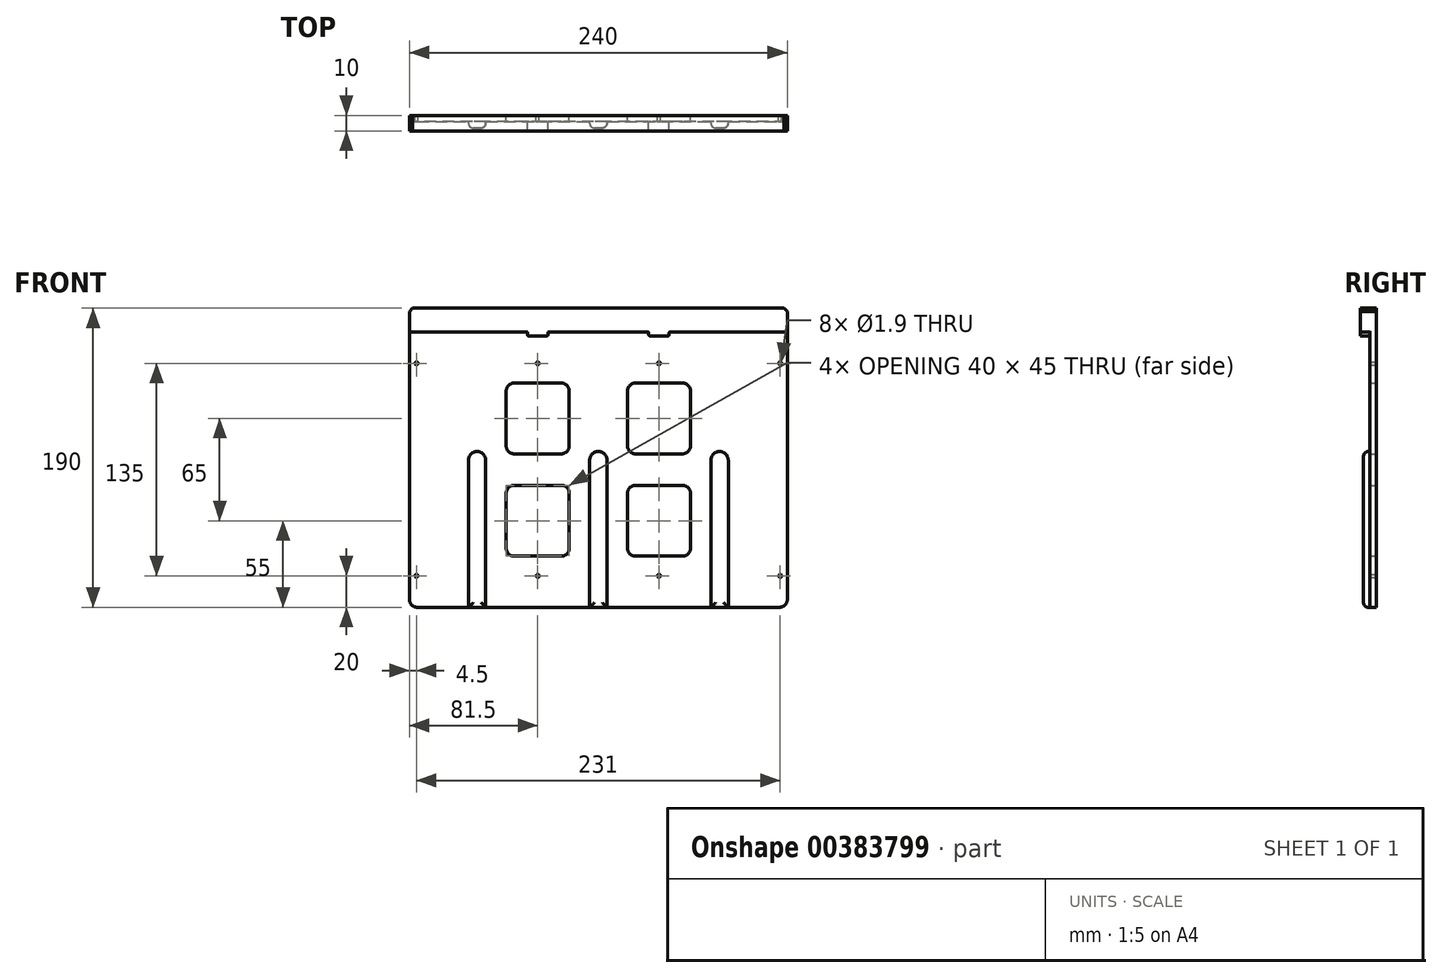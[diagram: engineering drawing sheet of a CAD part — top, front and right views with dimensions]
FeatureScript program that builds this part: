
annotation { "Feature Type Name" : "Feature", "Feature Type Description" : "" }
export const myFeature = defineFeature(function(context is Context, id is Id, definition is map)
    precondition{}
    {
        {
            var Q0;
            Q0=qCreatedBy(makeId("Front.planeOp"),FACE);
            var sketch = newSketch(context, id + "F0", { "sketchPlane" : qUnion([Q0])});
            skLineSegment(sketch, "E0.bottom", {"start": v(0, 0) * mm, "end": v(240, 0) * mm});
            skLineSegment(sketch, "E0.top", {"start": v(0, 190) * mm, "end": v(240, 190) * mm});
            skLineSegment(sketch, "E0.left", {"start": v(0, 0) * mm, "end": v(0, 190) * mm});
            skLineSegment(sketch, "E0.right", {"start": v(240, 0) * mm, "end": v(240, 190) * mm});
            skLineSegment(sketch, "E1", {"start": v(120, 190) * mm, "end": v(120, 0) * mm, "construction": true});
            skLineSegment(sketch, "E2", {"start": v(197, 190) * mm, "end": v(197, 0) * mm, "construction": true});
            skLineSegment(sketch, "E3", {"start": v(43, 190) * mm, "end": v(43, 0) * mm, "construction": true});
            skArc(sketch, "E4", {"start": v(48.5, 93.5) * mm, "mid": v(43, 99) * mm, "end": v(37.5, 93.5) * mm});
            skArc(sketch, "E5", {"start": v(125.5, 93.5) * mm, "mid": v(120, 99) * mm, "end": v(114.5, 93.5) * mm});
            skArc(sketch, "E6", {"start": v(202.5, 93.5) * mm, "mid": v(197, 99) * mm, "end": v(191.5, 93.5) * mm});
            skLineSegment(sketch, "E7", {"start": v(81.5, 190) * mm, "end": v(81.5, 0) * mm, "construction": true});
            skLineSegment(sketch, "E8", {"start": v(158.5, 190) * mm, "end": v(158.5, 0) * mm, "construction": true});
            skPoint(sketch, "E9.middle", {"position": v(81.5, 0) * mm});
            skLineSegment(sketch, "E10", {"start": v(37.5, 93.5) * mm, "end": v(37.5, 0) * mm});
            skLineSegment(sketch, "E11", {"start": v(48.5, 93.5) * mm, "end": v(48.5, 0) * mm});
            skLineSegment(sketch, "E12", {"start": v(114.5, 93.5) * mm, "end": v(114.5, 0) * mm});
            skLineSegment(sketch, "E13", {"start": v(125.5, 93.5) * mm, "end": v(125.5, 0) * mm});
            skLineSegment(sketch, "E14", {"start": v(191.5, 93.5) * mm, "end": v(191.5, 0) * mm});
            skLineSegment(sketch, "E15", {"start": v(202.5, 93.5) * mm, "end": v(202.5, 0) * mm});
            skLineSegment(sketch, "E16", {"start": v(0, 175) * mm, "end": v(240, 175) * mm, "construction": true});
            skLineSegment(sketch, "E17", {"start": v(75, 190) * mm, "end": v(75, 172.5) * mm});
            skLineSegment(sketch, "E18", {"start": v(75, 172.5) * mm, "end": v(88, 172.5) * mm});
            skLineSegment(sketch, "E19", {"start": v(88, 172.5) * mm, "end": v(88, 190) * mm});
            skLineSegment(sketch, "E20", {"start": v(152, 190) * mm, "end": v(152, 172.5) * mm});
            skLineSegment(sketch, "E21", {"start": v(152, 172.5) * mm, "end": v(165, 172.5) * mm});
            skLineSegment(sketch, "E22", {"start": v(165, 172.5) * mm, "end": v(165, 190) * mm});
            skLineSegment(sketch, "E23", {"start": v(235.5, 190) * mm, "end": v(235.5, 0) * mm, "construction": true});
            skLineSegment(sketch, "E24", {"start": v(4.5, 190) * mm, "end": v(4.5, 0) * mm, "construction": true});
            skCircle(sketch, "E25", {"center": v(4.5, 155) * mm, "radius": 0.95 * mm});
            skCircle(sketch, "E26", {"center": v(81.5, 155) * mm, "radius": 0.95 * mm});
            skCircle(sketch, "E27", {"center": v(158.5, 155) * mm, "radius": 0.95 * mm});
            skCircle(sketch, "E28", {"center": v(235.5, 155) * mm, "radius": 0.95 * mm});
            skCircle(sketch, "E29", {"center": v(4.5, 20) * mm, "radius": 0.95 * mm});
            skCircle(sketch, "E30", {"center": v(81.5, 20) * mm, "radius": 0.95 * mm});
            skCircle(sketch, "E31", {"center": v(158.5, 20) * mm, "radius": 0.95 * mm});
            skCircle(sketch, "E32", {"center": v(235.5, 20) * mm, "radius": 0.95 * mm});
            skLineSegment(sketch, "E33.bottom", {"start": v(101.5, 32.5) * mm, "end": v(61.5, 32.5) * mm});
            skLineSegment(sketch, "E33.top", {"start": v(101.5, 77.5) * mm, "end": v(61.5, 77.5) * mm});
            skLineSegment(sketch, "E33.left", {"start": v(101.5, 32.5) * mm, "end": v(101.5, 77.5) * mm});
            skLineSegment(sketch, "E33.right", {"start": v(61.5, 32.5) * mm, "end": v(61.5, 77.5) * mm});
            skPoint(sketch, "E33.middle", {"position": v(81.5, 55) * mm});
            skLineSegment(sketch, "E34.bottom", {"start": v(178.5, 32.5) * mm, "end": v(138.5, 32.5) * mm});
            skLineSegment(sketch, "E34.top", {"start": v(178.5, 77.5) * mm, "end": v(138.5, 77.5) * mm});
            skLineSegment(sketch, "E34.left", {"start": v(178.5, 32.5) * mm, "end": v(178.5, 77.5) * mm});
            skLineSegment(sketch, "E34.right", {"start": v(138.5, 32.5) * mm, "end": v(138.5, 77.5) * mm});
            skPoint(sketch, "E34.middle", {"position": v(158.5, 55) * mm});
            skLineSegment(sketch, "E35", {"start": v(0, 175) * mm, "end": v(75, 175) * mm});
            skLineSegment(sketch, "E36", {"start": v(88, 175) * mm, "end": v(152, 175) * mm});
            skLineSegment(sketch, "E37", {"start": v(165, 175) * mm, "end": v(240, 175) * mm});
            skLineSegment(sketch, "E38.bottom", {"start": v(101.5, 97.5) * mm, "end": v(61.5, 97.5) * mm});
            skLineSegment(sketch, "E38.top", {"start": v(101.5, 142.5) * mm, "end": v(61.5, 142.5) * mm});
            skLineSegment(sketch, "E38.left", {"start": v(101.5, 97.5) * mm, "end": v(101.5, 142.5) * mm});
            skLineSegment(sketch, "E38.right", {"start": v(61.5, 97.5) * mm, "end": v(61.5, 142.5) * mm});
            skPoint(sketch, "E38.middle", {"position": v(81.5, 120) * mm});
            skLineSegment(sketch, "E39.bottom", {"start": v(178.5, 97.5) * mm, "end": v(138.5, 97.5) * mm});
            skLineSegment(sketch, "E39.top", {"start": v(178.5, 142.5) * mm, "end": v(138.5, 142.5) * mm});
            skLineSegment(sketch, "E39.left", {"start": v(178.5, 97.5) * mm, "end": v(178.5, 142.5) * mm});
            skLineSegment(sketch, "E39.right", {"start": v(138.5, 97.5) * mm, "end": v(138.5, 142.5) * mm});
            skPoint(sketch, "E39.middle", {"position": v(158.5, 120) * mm});
            skSolve(sketch);
        }
        {
            var Q0;
            Q0=makeQuery(id+"F0.imprint","IMPRINT",FACE,{"disambiguationData":[TD([[makeQuery(id+"F0.imprint","IMPRINT",EDGE,{"derivedFrom":sQuery(id+"F0.wireOp",EDGE,"UCS8DdOD-ejyU-XilF-WruS-Bu7MYvNURBZs.bottom")}),-1.0]])]});
            var Q1;
            Q1=makeQuery(id+"F0.imprint","IMPRINT",FACE,{"disambiguationData":[TD([[makeQuery(id+"F0.imprint","IMPRINT",EDGE,{"derivedFrom":sQuery(id+"F0.wireOp",EDGE,"GRi4C73z-JWEP-kZG7-aWlK-krMTq5qBCM59.left")}),1.0]])]});
            var Q2;
            Q2=makeQuery(id+"F0.imprint","IMPRINT",FACE,{"disambiguationData":[TD([[makeQuery(id+"F0.imprint","IMPRINT",EDGE,{"derivedFrom":sQuery(id+"F0.wireOp",EDGE,"MJb00YoJ-KujM-1005-5pBj-Hys14JhzmI4w.left")}),1.0]])]});
            var Q3;
            Q3=makeQuery(id+"F0.imprint","IMPRINT",FACE,{"disambiguationData":[TD([[makeQuery(id+"F0.imprint","IMPRINT",EDGE,{"derivedFrom":sQuery(id+"F0.wireOp",EDGE,"MJb00YoJ-KujM-1005-5pBj-Hys14JhzmI4w.left")}),-1.0]])]});
            var Q4;
            Q4=makeQuery(id+"F0.imprint","IMPRINT",FACE,{"disambiguationData":[TD([[makeQuery(id+"F0.imprint","IMPRINT",EDGE,{"derivedFrom":sQuery(id+"F0.wireOp",EDGE,"SsHJZUVz-7gaE-nAlA-kBK5-nGGxjkbp80cZ.bottom")}),-1.0]])]});
            var Q5;
            {var subQ1=sQuery(id+"F0.wireOp",EDGE,"E0.right");Q5=makeQuery(id+"F0.imprint","IMPRINT",FACE,{"disambiguationData":[TD([[makeQuery(id+"F0.imprint","IMPRINT",EDGE,{"derivedFrom":subQ1}),1.0]])]});}
            var Q6;
            Q6=makeQuery(id+"F0.imprint","IMPRINT",FACE,{"disambiguationData":[TD([[makeQuery(id+"F0.imprint","IMPRINT",EDGE,{"derivedFrom":sQuery(id+"F0.wireOp",EDGE,"cF3qAKgA-6R1k-92Ln-ywlv-DPr7yGT8WVYd.left")}),1.0]])]});
            var Q7;
            {var subQ0=sQuery(id+"F0.wireOp",EDGE,"NWw21f8w-tgmn-euQu-w0p8-71T6GpV76rU4");Q7=makeQuery(id+"F0.imprint","IMPRINT",FACE,{"disambiguationData":[TD([[makeQuery(id+"F0.imprint","IMPRINT",EDGE,{"derivedFrom":subQ0}),-1.0]])]});}
            var Q8;
            {var subQ5=sQuery(id+"F0.wireOp",EDGE,"RuvmBQSr-5Cpm-upig-CqbM-MJYItVKPMDrs.bottom");Q8=makeQuery(id+"F0.imprint","IMPRINT",FACE,{"disambiguationData":[TD([[makeQuery(id+"F0.imprint","IMPRINT",EDGE,{"derivedFrom":subQ5}),1.0]])]});}
            var Q9;
            {var subQ5=sQuery(id+"F0.wireOp",EDGE,"E9.bottom");Q9=makeQuery(id+"F0.imprint","IMPRINT",FACE,{"disambiguationData":[TD([[makeQuery(id+"F0.imprint","IMPRINT",EDGE,{"derivedFrom":subQ5}),1.0]])]});}
            var Q10;
            Q10=makeQuery(id+"F0.imprint","IMPRINT",FACE,{"disambiguationData":[TD([[makeQuery(id+"F0.imprint","IMPRINT",EDGE,{"derivedFrom":sQuery(id+"F0.wireOp",EDGE,"XTZR7JBc-rO7E-wzYZ-XdEQ-IZ1jBMIKU54G.bottom")}),-1.0]])]});
            var Q11;
            Q11=makeQuery(id+"F0.imprint","IMPRINT",FACE,{"disambiguationData":[TD([[makeQuery(id+"F0.imprint","IMPRINT",EDGE,{"derivedFrom":sQuery(id+"F0.wireOp",EDGE,"QuKBfMWp-nAjc-eiIa-FsoC-LC1ooK1glI0I.bottom")}),-1.0]])]});
            var Q12;
            Q12=makeQuery(id+"F0.imprint","IMPRINT",FACE,{"disambiguationData":[TD([[makeQuery(id+"F0.imprint","IMPRINT",EDGE,{"derivedFrom":sQuery(id+"F0.wireOp",EDGE,"zr7SBste-XHF5-nfNJ-ePE3-pIRu4rkJVY1c.bottom")}),-1.0]])]});
            var Q13;
            Q13=makeQuery(id+"F0.imprint","IMPRINT",FACE,{"disambiguationData":[TD([[makeQuery(id+"F0.imprint","IMPRINT",EDGE,{"derivedFrom":sQuery(id+"F0.wireOp",EDGE,"EneNzpn4-2OMr-KFmW-9g9d-3BS7Mlzjb1r9.bottom")}),-1.0]])]});
            var Q14;
            {var subQ0=sQuery(id+"F0.wireOp",EDGE,"mL9XTioa-9DpA-IpuZ-Q8Eg-WP72gxXpwuHZ.bottom");var subQ1=sQuery(id+"F0.wireOp",EDGE,"SsHJZUVz-7gaE-nAlA-kBK5-nGGxjkbp80cZ.left");var subQ2=makeQuery(id+"F0.imprint","INTERSECT",VERTEX,{"derivedFrom":[subQ1,subQ0]});Q14=makeQuery(id+"F0.imprint","IMPRINT",FACE,{"disambiguationData":[TD([[makeQuery(id+"F0.imprint","IMPRINT",EDGE,{"disambiguationData":[TD([[subQ2,-1.0]])],"derivedFrom":subQ1}),-1.0]])]});}
            var Q15;
            {var subQ5=sQuery(id+"F0.wireOp",EDGE,"m287s5nx-l1Bl-8Bmj-dwCZ-KAfyaVMRRT36.top");Q15=makeQuery(id+"F0.imprint","IMPRINT",FACE,{"disambiguationData":[TD([[makeQuery(id+"F0.imprint","IMPRINT",EDGE,{"derivedFrom":subQ5}),-1.0]])]});}
            var Q16;
            {var subQ5=sQuery(id+"F0.wireOp",EDGE,"mL9XTioa-9DpA-IpuZ-Q8Eg-WP72gxXpwuHZ.left");Q16=makeQuery(id+"F0.imprint","IMPRINT",FACE,{"disambiguationData":[TD([[makeQuery(id+"F0.imprint","IMPRINT",EDGE,{"derivedFrom":subQ5}),1.0]])]});}
            var Q17;
            {var subQ0=sQuery(id+"F0.wireOp",EDGE,"mL9XTioa-9DpA-IpuZ-Q8Eg-WP72gxXpwuHZ.bottom");var subQ1=sQuery(id+"F0.wireOp",EDGE,"SsHJZUVz-7gaE-nAlA-kBK5-nGGxjkbp80cZ.left");var subQ2=makeQuery(id+"F0.imprint","INTERSECT",VERTEX,{"derivedFrom":[subQ1,subQ0]});Q17=makeQuery(id+"F0.imprint","IMPRINT",FACE,{"disambiguationData":[TD([[makeQuery(id+"F0.imprint","IMPRINT",EDGE,{"disambiguationData":[TD([[subQ2,-1.0]])],"derivedFrom":subQ1}),1.0]])]});}
            var Q18;
            {var subQ3=sQuery(id+"F0.wireOp",EDGE,"8tIIhmZ9-kIaI-KP0b-BDpp-fG9OmIQPOIbA.top");Q18=makeQuery(id+"F0.imprint","IMPRINT",FACE,{"disambiguationData":[TD([[makeQuery(id+"F0.imprint","IMPRINT",EDGE,{"derivedFrom":subQ3}),-1.0]])]});}
            var Q19;
            {var subQ5=sQuery(id+"F0.wireOp",EDGE,"mL9XTioa-9DpA-IpuZ-Q8Eg-WP72gxXpwuHZ.right");Q19=makeQuery(id+"F0.imprint","IMPRINT",FACE,{"disambiguationData":[TD([[makeQuery(id+"F0.imprint","IMPRINT",EDGE,{"derivedFrom":subQ5}),-1.0]])]});}
            var Q20;
            Q20=makeQuery(id+"F0.imprint","IMPRINT",FACE,{"disambiguationData":[TD([[makeQuery(id+"F0.imprint","IMPRINT",EDGE,{"derivedFrom":sQuery(id+"F0.wireOp",EDGE,"m287s5nx-l1Bl-8Bmj-dwCZ-KAfyaVMRRT36.bottom")}),-1.0]])]});
            var Q21;
            Q21=makeQuery(id+"F0.imprint","IMPRINT",FACE,{"disambiguationData":[TD([[makeQuery(id+"F0.imprint","IMPRINT",EDGE,{"derivedFrom":sQuery(id+"F0.wireOp",EDGE,"8tIIhmZ9-kIaI-KP0b-BDpp-fG9OmIQPOIbA.bottom")}),-1.0]])]});
            var Q22;
            {var subQ0=sQuery(id+"F0.wireOp",EDGE,"E20");var subQ1=sQuery(id+"F0.wireOp",EDGE,"E0.top");var subQ2=makeQuery(id+"F0.imprint","INTERSECT",VERTEX,{"derivedFrom":[subQ1,subQ0]});Q22=makeQuery(id+"F0.imprint","IMPRINT",FACE,{"disambiguationData":[TD([[makeQuery(id+"F0.imprint","IMPRINT",EDGE,{"disambiguationData":[TD([[subQ2,-1.0]])],"derivedFrom":subQ1}),-1.0]])]});}
            var Q23;
            {var subQ5=sQuery(id+"F0.wireOp",EDGE,"E21");Q23=makeQuery(id+"F0.imprint","IMPRINT",FACE,{"disambiguationData":[TD([[makeQuery(id+"F0.imprint","IMPRINT",EDGE,{"derivedFrom":subQ5}),1.0]])]});}
            var Q24;
            {var subQ0=sQuery(id+"F0.wireOp",EDGE,"E19");var subQ1=sQuery(id+"F0.wireOp",EDGE,"E0.top");var subQ2=makeQuery(id+"F0.imprint","INTERSECT",VERTEX,{"derivedFrom":[subQ1,subQ0]});Q24=makeQuery(id+"F0.imprint","IMPRINT",FACE,{"disambiguationData":[TD([[makeQuery(id+"F0.imprint","IMPRINT",EDGE,{"disambiguationData":[TD([[subQ2,-1.0]])],"derivedFrom":subQ1}),-1.0]])]});}
            var Q25;
            Q25=makeQuery(id+"F0.imprint","IMPRINT",FACE,{"disambiguationData":[TD([[makeQuery(id+"F0.imprint","IMPRINT",EDGE,{"derivedFrom":sQuery(id+"F0.wireOp",EDGE,"E4")}),-1.0]])]});
            var Q26;
            {var subQ5=sQuery(id+"F0.wireOp",EDGE,"E18");Q26=makeQuery(id+"F0.imprint","IMPRINT",FACE,{"disambiguationData":[TD([[makeQuery(id+"F0.imprint","IMPRINT",EDGE,{"derivedFrom":subQ5}),1.0]])]});}
            var Q27;
            {var subQ0=sQuery(id+"F0.wireOp",EDGE,"E17");var subQ1=sQuery(id+"F0.wireOp",EDGE,"E0.top");var subQ2=makeQuery(id+"F0.imprint","INTERSECT",VERTEX,{"derivedFrom":[subQ1,subQ0]});Q27=makeQuery(id+"F0.imprint","IMPRINT",FACE,{"disambiguationData":[TD([[makeQuery(id+"F0.imprint","IMPRINT",EDGE,{"disambiguationData":[TD([[subQ2,-1.0]])],"derivedFrom":subQ1}),-1.0]])]});}
            var Q28;
            {var subQ0=sQuery(id+"F0.wireOp",EDGE,"E0.left");var subQ1=sQuery(id+"F0.wireOp",EDGE,"E0.top");var subQ2=makeQuery(id+"F0.imprint","INTERSECT",VERTEX,{"derivedFrom":[subQ1,subQ0]});Q28=makeQuery(id+"F0.imprint","IMPRINT",FACE,{"disambiguationData":[TD([[makeQuery(id+"F0.imprint","IMPRINT",EDGE,{"disambiguationData":[TD([[subQ2,-1.0]])],"derivedFrom":subQ1}),-1.0]])]});}
            var Q29;
            Q29=makeQuery(id+"F0.imprint","IMPRINT",FACE,{"disambiguationData":[TD([[makeQuery(id+"F0.imprint","IMPRINT",EDGE,{"derivedFrom":sQuery(id+"F0.wireOp",EDGE,"E4")}),1.0]])]});
            var Q30;
            Q30=makeQuery(id+"F0.imprint","IMPRINT",FACE,{"disambiguationData":[TD([[makeQuery(id+"F0.imprint","IMPRINT",EDGE,{"derivedFrom":sQuery(id+"F0.wireOp",EDGE,"E5")}),1.0]])]});
            var Q31;
            Q31=makeQuery(id+"F0.imprint","IMPRINT",FACE,{"disambiguationData":[TD([[makeQuery(id+"F0.imprint","IMPRINT",EDGE,{"derivedFrom":sQuery(id+"F0.wireOp",EDGE,"E6")}),1.0]])]});
            extrude(context, id + "F1", {"entities" : qUnion([Q0, Q1, Q2, Q3, Q4, Q5, Q6, Q7, Q8, Q9, Q10, Q11, Q12, Q13, Q14, Q15, Q16, Q17, Q18, Q19, Q20, Q21, Q22, Q23, Q24, Q25, Q26, Q27, Q28, Q29, Q30, Q31]), "depth" : 4 * mm});
        }
        {
            var Q0;
            {var subQ0=sQuery(id+"F0.wireOp",EDGE,"mL9XTioa-9DpA-IpuZ-Q8Eg-WP72gxXpwuHZ.bottom");var subQ1=sQuery(id+"F0.wireOp",EDGE,"NWw21f8w-tgmn-euQu-w0p8-71T6GpV76rU4");var subQ2=makeQuery(id+"F0.imprint","INTERSECT",VERTEX,{"derivedFrom":[subQ1,subQ0]});Q0=makeQuery(id+"F0.imprint","IMPRINT",FACE,{"disambiguationData":[TD([[makeQuery(id+"F0.imprint","IMPRINT",EDGE,{"disambiguationData":[TD([[subQ2,-1.0]])],"derivedFrom":subQ1}),-1.0]])]});}
            var Q1;
            {var subQ5=sQuery(id+"F0.wireOp",EDGE,"m287s5nx-l1Bl-8Bmj-dwCZ-KAfyaVMRRT36.top");Q1=makeQuery(id+"F0.imprint","IMPRINT",FACE,{"disambiguationData":[TD([[makeQuery(id+"F0.imprint","IMPRINT",EDGE,{"derivedFrom":subQ5}),-1.0]])]});}
            var Q2;
            {var subQ5=sQuery(id+"F0.wireOp",EDGE,"mL9XTioa-9DpA-IpuZ-Q8Eg-WP72gxXpwuHZ.left");Q2=makeQuery(id+"F0.imprint","IMPRINT",FACE,{"disambiguationData":[TD([[makeQuery(id+"F0.imprint","IMPRINT",EDGE,{"derivedFrom":subQ5}),1.0]])]});}
            var Q3;
            {var subQ0=sQuery(id+"F0.wireOp",EDGE,"mL9XTioa-9DpA-IpuZ-Q8Eg-WP72gxXpwuHZ.bottom");var subQ1=sQuery(id+"F0.wireOp",EDGE,"SsHJZUVz-7gaE-nAlA-kBK5-nGGxjkbp80cZ.left");var subQ2=makeQuery(id+"F0.imprint","INTERSECT",VERTEX,{"derivedFrom":[subQ1,subQ0]});Q3=makeQuery(id+"F0.imprint","IMPRINT",FACE,{"disambiguationData":[TD([[makeQuery(id+"F0.imprint","IMPRINT",EDGE,{"disambiguationData":[TD([[subQ2,-1.0]])],"derivedFrom":subQ1}),-1.0]])]});}
            var Q4;
            {var subQ0=sQuery(id+"F0.wireOp",EDGE,"mL9XTioa-9DpA-IpuZ-Q8Eg-WP72gxXpwuHZ.bottom");var subQ1=sQuery(id+"F0.wireOp",EDGE,"SsHJZUVz-7gaE-nAlA-kBK5-nGGxjkbp80cZ.left");var subQ2=makeQuery(id+"F0.imprint","INTERSECT",VERTEX,{"derivedFrom":[subQ1,subQ0]});Q4=makeQuery(id+"F0.imprint","IMPRINT",FACE,{"disambiguationData":[TD([[makeQuery(id+"F0.imprint","IMPRINT",EDGE,{"disambiguationData":[TD([[subQ2,-1.0]])],"derivedFrom":subQ1}),1.0]])]});}
            var Q5;
            {var subQ3=sQuery(id+"F0.wireOp",EDGE,"8tIIhmZ9-kIaI-KP0b-BDpp-fG9OmIQPOIbA.top");Q5=makeQuery(id+"F0.imprint","IMPRINT",FACE,{"disambiguationData":[TD([[makeQuery(id+"F0.imprint","IMPRINT",EDGE,{"derivedFrom":subQ3}),-1.0]])]});}
            var Q6;
            {var subQ5=sQuery(id+"F0.wireOp",EDGE,"mL9XTioa-9DpA-IpuZ-Q8Eg-WP72gxXpwuHZ.right");Q6=makeQuery(id+"F0.imprint","IMPRINT",FACE,{"disambiguationData":[TD([[makeQuery(id+"F0.imprint","IMPRINT",EDGE,{"derivedFrom":subQ5}),-1.0]])]});}
            var Q7;
            {var subQ5=sQuery(id+"F0.wireOp",EDGE,"RuvmBQSr-5Cpm-upig-CqbM-MJYItVKPMDrs.bottom");Q7=makeQuery(id+"F0.imprint","IMPRINT",FACE,{"disambiguationData":[TD([[makeQuery(id+"F0.imprint","IMPRINT",EDGE,{"derivedFrom":subQ5}),1.0]])]});}
            var Q8;
            {var subQ5=sQuery(id+"F0.wireOp",EDGE,"E9.bottom");Q8=makeQuery(id+"F0.imprint","IMPRINT",FACE,{"disambiguationData":[TD([[makeQuery(id+"F0.imprint","IMPRINT",EDGE,{"derivedFrom":subQ5}),1.0]])]});}
            var Q9;
            Q9=makeQuery(id+"F0.imprint","IMPRINT",FACE,{"disambiguationData":[TD([[makeQuery(id+"F0.imprint","IMPRINT",EDGE,{"derivedFrom":sQuery(id+"F0.wireOp",EDGE,"MJb00YoJ-KujM-1005-5pBj-Hys14JhzmI4w.left")}),1.0]])]});
            var Q10;
            Q10=makeQuery(id+"F0.imprint","IMPRINT",FACE,{"disambiguationData":[TD([[makeQuery(id+"F0.imprint","IMPRINT",EDGE,{"derivedFrom":sQuery(id+"F0.wireOp",EDGE,"cF3qAKgA-6R1k-92Ln-ywlv-DPr7yGT8WVYd.left")}),1.0]])]});
            var Q11;
            Q11=makeQuery(id+"F0.imprint","IMPRINT",FACE,{"disambiguationData":[TD([[makeQuery(id+"F0.imprint","IMPRINT",EDGE,{"derivedFrom":sQuery(id+"F0.wireOp",EDGE,"GRi4C73z-JWEP-kZG7-aWlK-krMTq5qBCM59.left")}),1.0]])]});
            var Q12;
            Q12=makeQuery(id+"F0.imprint","IMPRINT",FACE,{"disambiguationData":[TD([[makeQuery(id+"F0.imprint","IMPRINT",EDGE,{"derivedFrom":sQuery(id+"F0.wireOp",EDGE,"E4")}),1.0]])]});
            var Q13;
            Q13=makeQuery(id+"F0.imprint","IMPRINT",FACE,{"disambiguationData":[TD([[makeQuery(id+"F0.imprint","IMPRINT",EDGE,{"derivedFrom":sQuery(id+"F0.wireOp",EDGE,"E5")}),1.0]])]});
            var Q14;
            Q14=makeQuery(id+"F0.imprint","IMPRINT",FACE,{"disambiguationData":[TD([[makeQuery(id+"F0.imprint","IMPRINT",EDGE,{"derivedFrom":sQuery(id+"F0.wireOp",EDGE,"E6")}),1.0]])]});
            var Q15;
            Q15=sQuery(id+"F0.wireOp",EDGE,"GRi4C73z-JWEP-kZG7-aWlK-krMTq5qBCM59.right");
            var Q16;
            Q16=sQuery(id+"F0.wireOp",EDGE,"E4");
            var Q17;
            Q17=sQuery(id+"F0.wireOp",EDGE,"GRi4C73z-JWEP-kZG7-aWlK-krMTq5qBCM59.left");
            var Q18;
            Q18=sQuery(id+"F0.wireOp",EDGE,"cZHNsq4v-RjbF-qvnB-klJb-ReqYlpQdkK8d");
            var Q19;
            Q19=sQuery(id+"F0.wireOp",EDGE,"WpUKDbhN-TVkI-Cn0c-r8IW-TSZfF7SMHj3x");
            extrude(context, id + "F2", {"entities" : qUnion([Q0, Q1, Q2, Q3, Q4, Q5, Q6, Q7, Q8, Q9, Q10, Q11, Q12, Q13, Q14]), "operationType" : NewBodyOperationType.ADD, "surfaceEntities" : qUnion([Q15, Q16, Q17, Q18, Q19]), "depth" : 8 * mm});
        }
        {
            var Q0;
            {var subQ0=sQuery(id+"F0.wireOp",EDGE,"E17");var subQ1=sQuery(id+"F0.wireOp",EDGE,"E0.top");var subQ2=makeQuery(id+"F0.imprint","INTERSECT",VERTEX,{"derivedFrom":[subQ1,subQ0]});Q0=makeQuery(id+"F0.imprint","IMPRINT",FACE,{"disambiguationData":[TD([[makeQuery(id+"F0.imprint","IMPRINT",EDGE,{"disambiguationData":[TD([[subQ2,-1.0]])],"derivedFrom":subQ1}),-1.0]])]});}
            var Q1;
            {var subQ5=sQuery(id+"F0.wireOp",EDGE,"E18");Q1=makeQuery(id+"F0.imprint","IMPRINT",FACE,{"disambiguationData":[TD([[makeQuery(id+"F0.imprint","IMPRINT",EDGE,{"derivedFrom":subQ5}),1.0]])]});}
            var Q2;
            {var subQ5=sQuery(id+"F0.wireOp",EDGE,"E21");Q2=makeQuery(id+"F0.imprint","IMPRINT",FACE,{"disambiguationData":[TD([[makeQuery(id+"F0.imprint","IMPRINT",EDGE,{"derivedFrom":subQ5}),1.0]])]});}
            var Q3;
            {var subQ0=sQuery(id+"F0.wireOp",EDGE,"E20");var subQ1=sQuery(id+"F0.wireOp",EDGE,"E0.top");var subQ2=makeQuery(id+"F0.imprint","INTERSECT",VERTEX,{"derivedFrom":[subQ1,subQ0]});Q3=makeQuery(id+"F0.imprint","IMPRINT",FACE,{"disambiguationData":[TD([[makeQuery(id+"F0.imprint","IMPRINT",EDGE,{"disambiguationData":[TD([[subQ2,-1.0]])],"derivedFrom":subQ1}),-1.0]])]});}
            var Q4;
            {var subQ5=sQuery(id+"F0.wireOp",EDGE,"E37");Q4=makeQuery(id+"F0.imprint","IMPRINT",FACE,{"disambiguationData":[TD([[makeQuery(id+"F0.imprint","IMPRINT",EDGE,{"derivedFrom":subQ5}),1.0]])]});}
            var Q5;
            {var subQ5=sQuery(id+"F0.wireOp",EDGE,"E36");Q5=makeQuery(id+"F0.imprint","IMPRINT",FACE,{"disambiguationData":[TD([[makeQuery(id+"F0.imprint","IMPRINT",EDGE,{"derivedFrom":subQ5}),1.0]])]});}
            var Q6;
            {var subQ5=sQuery(id+"F0.wireOp",EDGE,"E35");Q6=makeQuery(id+"F0.imprint","IMPRINT",FACE,{"disambiguationData":[TD([[makeQuery(id+"F0.imprint","IMPRINT",EDGE,{"derivedFrom":subQ5}),1.0]])]});}
            extrude(context, id + "F3", {"entities" : qUnion([Q0, Q1, Q2, Q3, Q4, Q5, Q6]), "operationType" : NewBodyOperationType.ADD, "depth" : 10 * mm});
        }
        {
            var Q0;
            Q0=makeQuery(id+"F1.opExtrude","SWEPT_EDGE",EDGE,{"disambiguationData":[OSD([sQuery(id+"F0.wireOp",EDGE,"E0.bottom"),sQuery(id+"F0.wireOp",EDGE,"E0.left")])]});
            var Q1;
            Q1=makeQuery(id+"F1.opExtrude","SWEPT_EDGE",EDGE,{"disambiguationData":[OSD([sQuery(id+"F0.wireOp",EDGE,"E0.bottom"),sQuery(id+"F0.wireOp",EDGE,"E0.right")])]});
            var Q2;
            Q2=makeQuery(id+"F1.opExtrude","SWEPT_EDGE",EDGE,{"disambiguationData":[OSD([sQuery(id+"F0.wireOp",EDGE,"E34.bottom"),sQuery(id+"F0.wireOp",EDGE,"E34.right")])]});
            var Q3;
            Q3=makeQuery(id+"F1.opExtrude","SWEPT_EDGE",EDGE,{"disambiguationData":[OSD([sQuery(id+"F0.wireOp",EDGE,"E34.bottom"),sQuery(id+"F0.wireOp",EDGE,"E34.left")])]});
            var Q4;
            Q4=makeQuery(id+"F1.opExtrude","SWEPT_EDGE",EDGE,{"disambiguationData":[OSD([sQuery(id+"F0.wireOp",EDGE,"E34.top"),sQuery(id+"F0.wireOp",EDGE,"E34.left")])]});
            var Q5;
            Q5=makeQuery(id+"F1.opExtrude","SWEPT_EDGE",EDGE,{"disambiguationData":[OSD([sQuery(id+"F0.wireOp",EDGE,"E34.top"),sQuery(id+"F0.wireOp",EDGE,"E34.right")])]});
            var Q6;
            Q6=makeQuery(id+"F1.opExtrude","SWEPT_EDGE",EDGE,{"disambiguationData":[OSD([sQuery(id+"F0.wireOp",EDGE,"E39.top"),sQuery(id+"F0.wireOp",EDGE,"E39.right")])]});
            var Q7;
            Q7=makeQuery(id+"F1.opExtrude","SWEPT_EDGE",EDGE,{"disambiguationData":[OSD([sQuery(id+"F0.wireOp",EDGE,"E39.top"),sQuery(id+"F0.wireOp",EDGE,"E39.left")])]});
            var Q8;
            Q8=makeQuery(id+"F1.opExtrude","SWEPT_EDGE",EDGE,{"disambiguationData":[OSD([sQuery(id+"F0.wireOp",EDGE,"E39.bottom"),sQuery(id+"F0.wireOp",EDGE,"E39.left")])]});
            var Q9;
            Q9=makeQuery(id+"F1.opExtrude","SWEPT_EDGE",EDGE,{"disambiguationData":[OSD([sQuery(id+"F0.wireOp",EDGE,"E39.bottom"),sQuery(id+"F0.wireOp",EDGE,"E39.right")])]});
            var Q10;
            Q10=makeQuery(id+"F1.opExtrude","SWEPT_EDGE",EDGE,{"disambiguationData":[OSD([sQuery(id+"F0.wireOp",EDGE,"E33.bottom"),sQuery(id+"F0.wireOp",EDGE,"E33.right")])]});
            var Q11;
            Q11=makeQuery(id+"F1.opExtrude","SWEPT_EDGE",EDGE,{"disambiguationData":[OSD([sQuery(id+"F0.wireOp",EDGE,"E33.bottom"),sQuery(id+"F0.wireOp",EDGE,"E33.left")])]});
            var Q12;
            Q12=makeQuery(id+"F1.opExtrude","SWEPT_EDGE",EDGE,{"disambiguationData":[OSD([sQuery(id+"F0.wireOp",EDGE,"E33.top"),sQuery(id+"F0.wireOp",EDGE,"E33.left")])]});
            var Q13;
            Q13=makeQuery(id+"F1.opExtrude","SWEPT_EDGE",EDGE,{"disambiguationData":[OSD([sQuery(id+"F0.wireOp",EDGE,"E33.top"),sQuery(id+"F0.wireOp",EDGE,"E33.right")])]});
            var Q14;
            Q14=makeQuery(id+"F1.opExtrude","SWEPT_EDGE",EDGE,{"disambiguationData":[OSD([sQuery(id+"F0.wireOp",EDGE,"E38.bottom"),sQuery(id+"F0.wireOp",EDGE,"E38.left")])]});
            var Q15;
            Q15=makeQuery(id+"F1.opExtrude","SWEPT_EDGE",EDGE,{"disambiguationData":[OSD([sQuery(id+"F0.wireOp",EDGE,"E38.top"),sQuery(id+"F0.wireOp",EDGE,"E38.left")])]});
            var Q16;
            Q16=makeQuery(id+"F1.opExtrude","SWEPT_EDGE",EDGE,{"disambiguationData":[OSD([sQuery(id+"F0.wireOp",EDGE,"E38.top"),sQuery(id+"F0.wireOp",EDGE,"E38.right")])]});
            var Q17;
            Q17=makeQuery(id+"F1.opExtrude","SWEPT_EDGE",EDGE,{"disambiguationData":[OSD([sQuery(id+"F0.wireOp",EDGE,"E38.bottom"),sQuery(id+"F0.wireOp",EDGE,"E38.right")])]});
            fillet(context, id + "F4", {"entities" : qUnion([Q0, Q1, Q2, Q3, Q4, Q5, Q6, Q7, Q8, Q9, Q10, Q11, Q12, Q13, Q14, Q15, Q16, Q17]), "radius" : 5 * mm, "tangentPropagation" : true, "allowEdgeOverflow" : false});
        }
        {
            var Q0;
            {var subQ0=sQuery(id+"F0.wireOp",EDGE,"E0.right");var subQ1=sQuery(id+"F0.wireOp",EDGE,"E0.top");Q0=makeQuery(id+"F3.boolean.opBoolean","MERGE",EDGE,{"derivedFrom":[makeQuery(id+"F1.opExtrude","SWEPT_EDGE",EDGE,{"disambiguationData":[OSD([subQ1,subQ0])]}),makeQuery(id+"F3.opExtrude","SWEPT_EDGE",EDGE,{"disambiguationData":[OSD([subQ1,subQ0])]})]});}
            var Q1;
            {var subQ0=sQuery(id+"F0.wireOp",EDGE,"E0.left");var subQ1=sQuery(id+"F0.wireOp",EDGE,"E0.top");Q1=makeQuery(id+"F3.boolean.opBoolean","MERGE",EDGE,{"derivedFrom":[makeQuery(id+"F1.opExtrude","SWEPT_EDGE",EDGE,{"disambiguationData":[OSD([subQ1,subQ0])]}),makeQuery(id+"F3.opExtrude","SWEPT_EDGE",EDGE,{"disambiguationData":[OSD([subQ1,subQ0])]})]});}
            chamfer(context, id + "F5", {"entities" : qUnion([Q0, Q1]), "width" : 2 * mm, "tangentPropagation" : true});
        }
        {
            var Q0;
            Q0=makeQuery(id+"F2.opExtrude","CAP_FACE",FACE,{"disambiguationData":[OSD([sQuery(id+"F0.wireOp",EDGE,"E0.bottom"),sQuery(id+"F0.wireOp",EDGE,"E4"),sQuery(id+"F0.wireOp",EDGE,"E10"),sQuery(id+"F0.wireOp",EDGE,"E11")])],"isStart":false});
            var Q1;
            Q1=makeQuery(id+"F2.opExtrude","CAP_FACE",FACE,{"disambiguationData":[OSD([sQuery(id+"F0.wireOp",EDGE,"E0.bottom"),sQuery(id+"F0.wireOp",EDGE,"E5"),sQuery(id+"F0.wireOp",EDGE,"E12"),sQuery(id+"F0.wireOp",EDGE,"E13")])],"isStart":false});
            var Q2;
            Q2=makeQuery(id+"F2.opExtrude","CAP_FACE",FACE,{"disambiguationData":[OSD([sQuery(id+"F0.wireOp",EDGE,"E0.bottom"),sQuery(id+"F0.wireOp",EDGE,"E6"),sQuery(id+"F0.wireOp",EDGE,"E14"),sQuery(id+"F0.wireOp",EDGE,"E15")])],"isStart":false});
            fillet(context, id + "F6", {"entities" : qUnion([Q0, Q1, Q2]), "radius" : 3 * mm, "tangentPropagation" : true, "allowEdgeOverflow" : false});
        }
        {
            var Q0;
            Q0=makeQuery(id+"F3.opExtrude","SWEPT_EDGE",EDGE,{"disambiguationData":[OSD([sQuery(id+"F0.wireOp",EDGE,"E17"),sQuery(id+"F0.wireOp",EDGE,"E18")])]});
            var Q1;
            Q1=makeQuery(id+"F3.opExtrude","SWEPT_EDGE",EDGE,{"disambiguationData":[OSD([sQuery(id+"F0.wireOp",EDGE,"E17"),sQuery(id+"F0.wireOp",EDGE,"E35")])]});
            var Q2;
            Q2=makeQuery(id+"F3.opExtrude","SWEPT_EDGE",EDGE,{"disambiguationData":[OSD([sQuery(id+"F0.wireOp",EDGE,"E18"),sQuery(id+"F0.wireOp",EDGE,"E19")])]});
            var Q3;
            Q3=makeQuery(id+"F3.opExtrude","SWEPT_EDGE",EDGE,{"disambiguationData":[OSD([sQuery(id+"F0.wireOp",EDGE,"E19"),sQuery(id+"F0.wireOp",EDGE,"E36")])]});
            var Q4;
            Q4=makeQuery(id+"F3.opExtrude","SWEPT_EDGE",EDGE,{"disambiguationData":[OSD([sQuery(id+"F0.wireOp",EDGE,"E20"),sQuery(id+"F0.wireOp",EDGE,"E36")])]});
            var Q5;
            Q5=makeQuery(id+"F3.opExtrude","SWEPT_EDGE",EDGE,{"disambiguationData":[OSD([sQuery(id+"F0.wireOp",EDGE,"E20"),sQuery(id+"F0.wireOp",EDGE,"E21")])]});
            var Q6;
            Q6=makeQuery(id+"F3.opExtrude","SWEPT_EDGE",EDGE,{"disambiguationData":[OSD([sQuery(id+"F0.wireOp",EDGE,"E21"),sQuery(id+"F0.wireOp",EDGE,"E22")])]});
            var Q7;
            Q7=makeQuery(id+"F3.opExtrude","SWEPT_EDGE",EDGE,{"disambiguationData":[OSD([sQuery(id+"F0.wireOp",EDGE,"E22"),sQuery(id+"F0.wireOp",EDGE,"E37")])]});
            var Q8;
            Q8=makeQuery(id+"F3.opExtrude","SWEPT_EDGE",EDGE,{"disambiguationData":[OSD([sQuery(id+"F0.wireOp",EDGE,"E0.right"),sQuery(id+"F0.wireOp",EDGE,"E37")])]});
            var Q9;
            Q9=makeQuery(id+"F3.opExtrude","SWEPT_EDGE",EDGE,{"disambiguationData":[OSD([sQuery(id+"F0.wireOp",EDGE,"E0.left"),sQuery(id+"F0.wireOp",EDGE,"E35")])]});
            fillet(context, id + "F7", {"entities" : qUnion([Q0, Q1, Q2, Q3, Q4, Q5, Q6, Q7, Q8, Q9]), "radius" : .5 * mm, "tangentPropagation" : true, "allowEdgeOverflow" : false});
        }
    });
